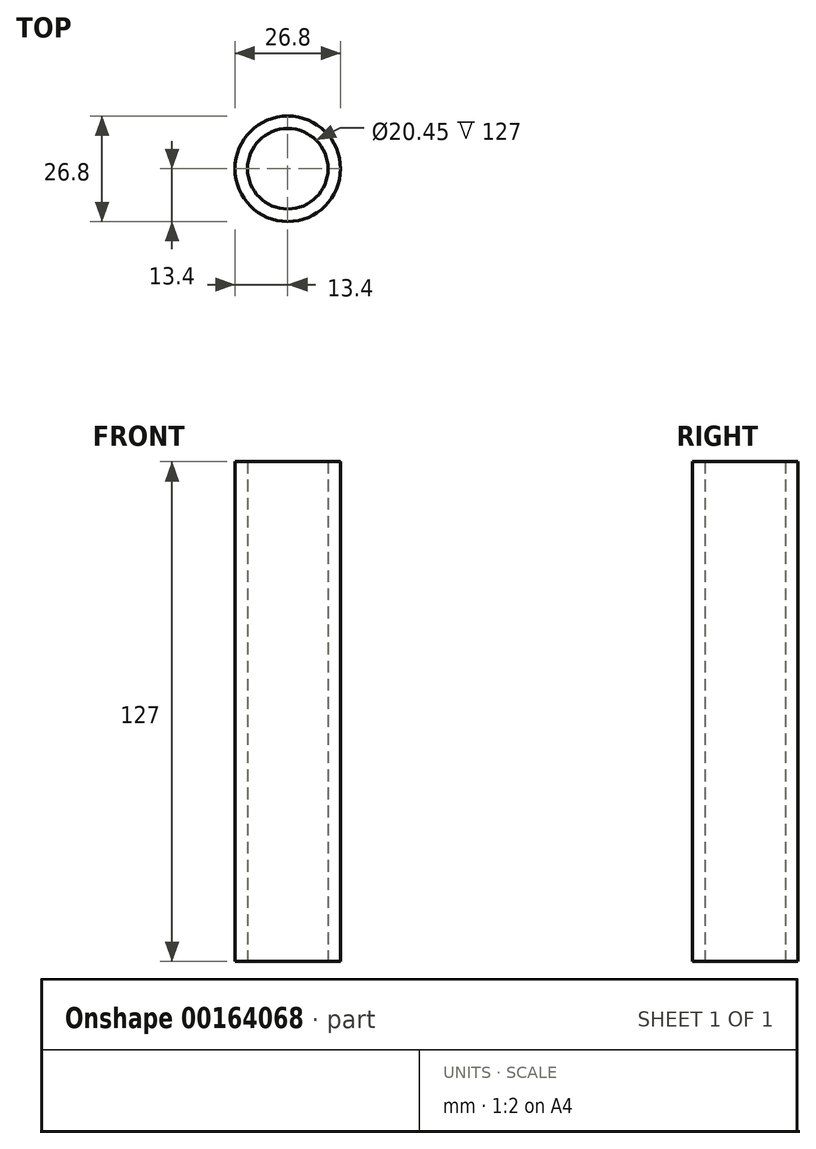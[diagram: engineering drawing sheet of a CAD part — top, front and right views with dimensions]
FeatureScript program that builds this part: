
annotation { "Feature Type Name" : "Feature", "Feature Type Description" : "" }
export const myFeature = defineFeature(function(context is Context, id is Id, definition is map)
    precondition{}
    {
        {
            var Q0;
            Q0=qCreatedBy(makeId("Top.planeOp"),FACE);
            var sketch = newSketch(context, id + "F0", { "sketchPlane" : qUnion([Q0])});
            skCircle(sketch, "E0", {"center": v(0, 0) * mm, "radius": 10.22 * mm});
            skCircle(sketch, "E1", {"center": v(0, 0) * mm, "radius": 13.4 * mm});
            skSolve(sketch);
        }
        {
            var Q0;
            Q0=makeQuery(id+"F0.imprint","IMPRINT",FACE,{"disambiguationData":[TD([[makeQuery(id+"F0.imprint","IMPRINT",EDGE,{"derivedFrom":sQuery(id+"F0.wireOp",EDGE,"E0")}),-1.0]])]});
            extrude(context, id + "F1", {"entities" : qUnion([Q0]), "depth" : 127 * mm, "offsetDistance" : 25.4 * mm});
        }
    });
